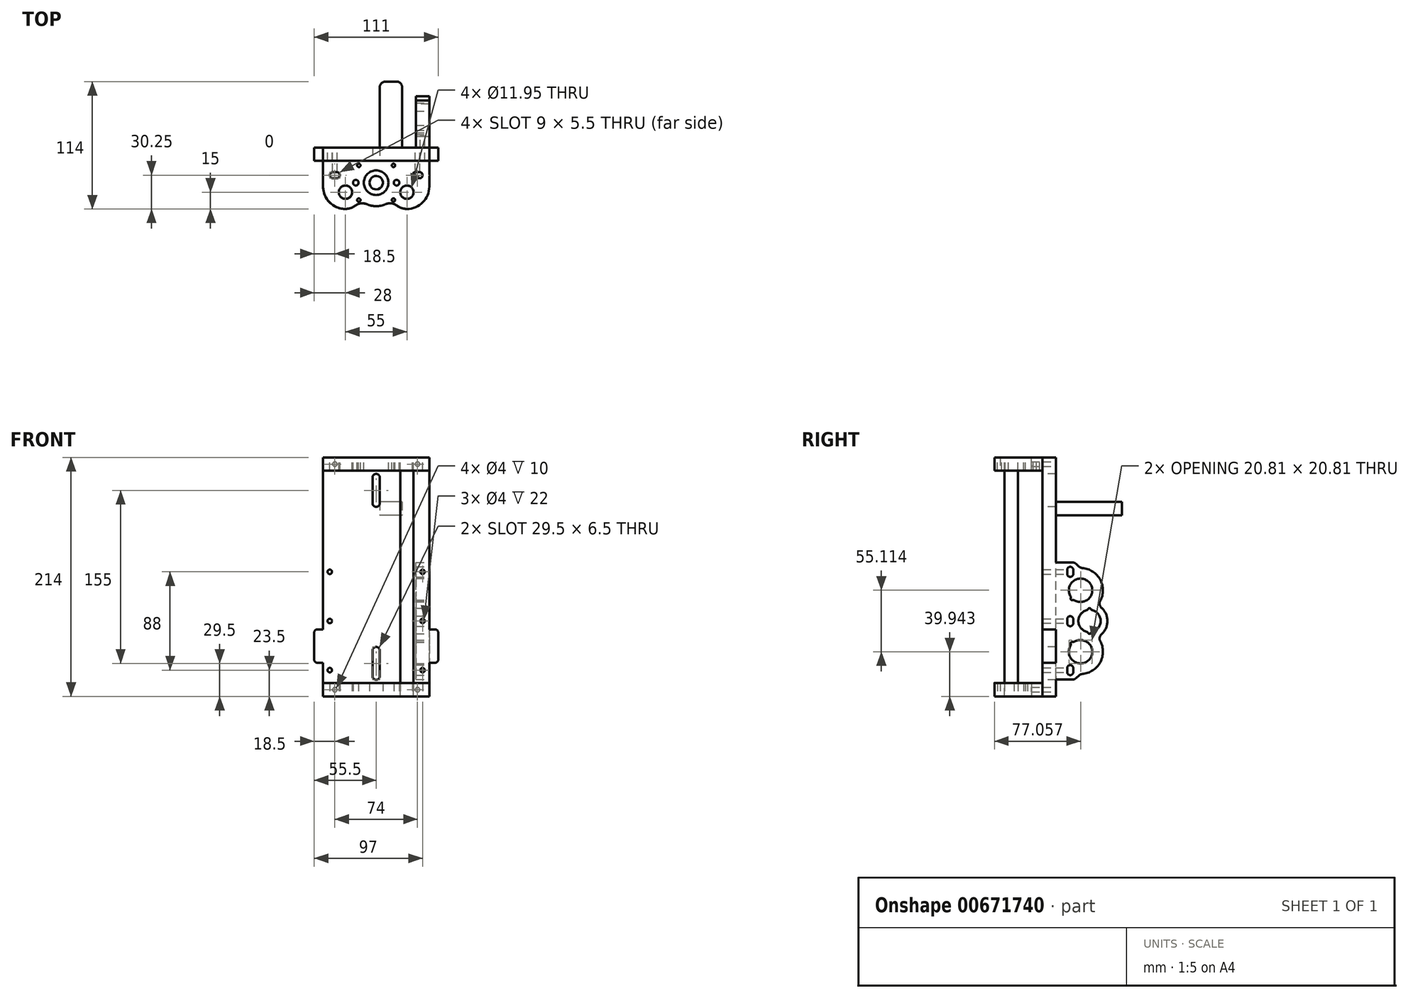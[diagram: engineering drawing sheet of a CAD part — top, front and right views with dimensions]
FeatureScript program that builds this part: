
annotation { "Feature Type Name" : "Feature", "Feature Type Description" : "" }
export const myFeature = defineFeature(function(context is Context, id is Id, definition is map)
    precondition{}
    {
        {
            assignVariable(context, id + "F0", {"name" : "L", "anyValue" : 214});
        }
        {
            var Q0;
            Q0=qCreatedBy(makeId("Front.planeOp"),FACE);
            var sketch = newSketch(context, id + "F1", { "sketchPlane" : qUnion([Q0])});
            skLineSegment(sketch, "E0.bottom", {"start": v(47.5, 0) * mm, "end": v(-47.5, 0) * mm});
            skLineSegment(sketch, "E0.top", {"start": v(-47.5, 214) * mm, "end": v(47.5, 214) * mm});
            skLineSegment(sketch, "E0.left", {"start": v(-47.5, 0) * mm, "end": v(-47.5, 214) * mm});
            skLineSegment(sketch, "E0.right", {"start": v(47.5, 0) * mm, "end": v(47.5, 214) * mm});
            skLineSegment(sketch, "E1.left", {"start": v(3.25, 196) * mm, "end": v(3.25, 173) * mm});
            skLineSegment(sketch, "E1.right", {"start": v(-3.25, 196) * mm, "end": v(-3.25, 173) * mm});
            skArc(sketch, "E2", {"start": v(3.25, 196) * mm, "mid": v(0, 199.25) * mm, "end": v(-3.25, 196) * mm});
            skArc(sketch, "E3", {"start": v(-3.25, 173) * mm, "mid": v(0, 169.75) * mm, "end": v(3.25, 173) * mm});
            skLineSegment(sketch, "E4", {"start": v(0, 214) * mm, "end": v(0, 196) * mm, "construction": true});
            skLineSegment(sketch, "E5.left", {"start": v(-3.25, 18) * mm, "end": v(-3.25, 41) * mm});
            skLineSegment(sketch, "E5.right", {"start": v(3.25, 18) * mm, "end": v(3.25, 41) * mm});
            skArc(sketch, "E6", {"start": v(-3.25, 18) * mm, "mid": v(0, 14.75) * mm, "end": v(3.25, 18) * mm});
            skArc(sketch, "E7", {"start": v(3.25, 41) * mm, "mid": v(0, 44.25) * mm, "end": v(-3.25, 41) * mm});
            skLineSegment(sketch, "E8", {"start": v(0, 0) * mm, "end": v(0, 18) * mm, "construction": true});
            skSolve(sketch);
        }
        {
            var Q0;
            Q0=qSketchRegion(id+"F1",true);
            extrude(context, id + "F2", {"entities" : qUnion([Q0]), "oppositeDirection" : true, "depth" : 12 * mm, "offsetDistance" : 25 * mm});
        }
        {
            var Q0;
            Q0=makeQuery(id+"F2.opExtrude","SWEPT_FACE",FACE,{"disambiguationData":[OSD([sQuery(id+"F1.wireOp",EDGE,"E0.top")])]});
            var sketch = newSketch(context, id + "F3", { "sketchPlane" : qUnion([Q0])});
            skLineSegment(sketch, "E9.bottom", {"start": v(-47.5, 0) * mm, "end": v(47.5, 0) * mm});
            skLineSegment(sketch, "E9.top", {"start": v(-27.5, -43) * mm, "end": v(27.5, -43) * mm, "construction": true});
            skLineSegment(sketch, "E9.left", {"start": v(-47.5, 0) * mm, "end": v(-47.5, -23) * mm});
            skLineSegment(sketch, "E9.right", {"start": v(47.5, 0) * mm, "end": v(47.5, -23) * mm});
            skLineSegment(sketch, "E10", {"start": v(0, 0) * mm, "end": v(0, -43) * mm, "construction": true});
            skCircle(sketch, "E11", {"center": v(-27.5, -28) * mm, "radius": 5.97 * mm});
            skCircle(sketch, "E12.MirrorC", {"center": v(27.5, -28) * mm, "radius": 5.97 * mm});
            skArc(sketch, "E13.filletArc", {"start": v(-47.5, -23) * mm, "mid": v(-41.64, -37.14) * mm, "end": v(-27.5, -43) * mm});
            skPoint(sketch, "E14.visualSharp", {"position": v(47.5, -43) * mm});
            skArc(sketch, "E14.filletArc", {"start": v(27.5, -43) * mm, "mid": v(41.64, -37.14) * mm, "end": v(47.5, -23) * mm});
            skCircle(sketch, "E15", {"center": v(0, -19.5) * mm, "radius": 11 * mm});
            skCircle(sketch, "E16", {"center": v(-18.25, -19.5) * mm, "radius": 2.5 * mm});
            skCircle(sketch, "E17.MirrorC", {"center": v(18.25, -19.5) * mm, "radius": 2.5 * mm});
            skLineSegment(sketch, "E18.bottom", {"start": v(-38.75, -10) * mm, "end": v(-35.25, -10) * mm});
            skLineSegment(sketch, "E18.top", {"start": v(-38.75, -15.5) * mm, "end": v(-35.25, -15.5) * mm});
            skArc(sketch, "E19", {"start": v(-38.75, -10) * mm, "mid": v(-41.5, -12.75) * mm, "end": v(-38.75, -15.5) * mm});
            skArc(sketch, "E20", {"start": v(-35.25, -15.5) * mm, "mid": v(-32.5, -12.75) * mm, "end": v(-35.25, -10) * mm});
            skLineSegment(sketch, "E21", {"start": v(-37, -10) * mm, "end": v(-37, -15.5) * mm, "construction": true});
            skArc(sketch, "E22.MirrorCS", {"start": v(35.25, -15.5) * mm, "mid": v(32.5, -12.75) * mm, "end": v(35.25, -10) * mm});
            skLineSegment(sketch, "E23.MirrorCS", {"start": v(38.75, -15.5) * mm, "end": v(35.25, -15.5) * mm});
            skLineSegment(sketch, "E24.MirrorCS", {"start": v(38.75, -10) * mm, "end": v(35.25, -10) * mm});
            skArc(sketch, "E25.MirrorCS", {"start": v(38.75, -10) * mm, "mid": v(41.5, -12.75) * mm, "end": v(38.75, -15.5) * mm});
            skArc(sketch, "E26", {"start": v(-7.8, 0) * mm, "mid": v(0, -40.5) * mm, "end": v(7.8, 0) * mm});
            skCircle(sketch, "E27", {"center": v(-27.5, -28) * mm, "radius": 15 * mm});
            skCircle(sketch, "E28", {"center": v(27.5, -28) * mm, "radius": 15 * mm});
            skSolve(sketch);
        }
        {
            var Q0;
            Q0=qSketchRegion(id+"F3",true);
            extrude(context, id + "F4", {"entities" : qUnion([Q0]), "oppositeDirection" : true, "depth" : 12 * mm, "offsetDistance" : 25 * mm});
        }
        {
            var Q0;
            Q0=makeQuery(id+"F4.opExtrude","SWEPT_EDGE",EDGE,{"disambiguationData":[OSD([sQuery(id+"F3.wireOp",EDGE,"E26"),sQuery(id+"F3.wireOp",EDGE,"E27")])]});
            var Q1;
            Q1=makeQuery(id+"F4.opExtrude","SWEPT_EDGE",EDGE,{"disambiguationData":[OSD([sQuery(id+"F3.wireOp",EDGE,"E26"),sQuery(id+"F3.wireOp",EDGE,"E28")])]});
            fillet(context, id + "F5", {"entities" : qUnion([Q0, Q1]), "radius" : 10 * mm, "tangentPropagation" : true, "allowEdgeOverflow" : false});
        }
        {
            var Q0;
            Q0=makeQuery(id+"F4.opExtrude","CAP_FACE",FACE,{"disambiguationData":[OSD([sQuery(id+"F3.wireOp",EDGE,"E9.bottom"),sQuery(id+"F3.wireOp",EDGE,"E9.top"),sQuery(id+"F3.wireOp",EDGE,"E9.left"),sQuery(id+"F3.wireOp",EDGE,"E9.right"),sQuery(id+"F3.wireOp",EDGE,"E11"),sQuery(id+"F3.wireOp",EDGE,"E12.MirrorC"),sQuery(id+"F3.wireOp",EDGE,"E13.filletArc"),sQuery(id+"F3.wireOp",EDGE,"E14.filletArc")])],"isStart":true});
            var sketch = newSketch(context, id + "F6", { "sketchPlane" : qUnion([Q0])});
            skCircle(sketch, "E29", {"center": v(27.5, -28) * mm, "radius": 6 * mm});
            skSolve(sketch);
        }
        {
            var Q0;
            Q0=qSketchRegion(id+"F6",true);
            extrude(context, id + "F7", {"entities" : qUnion([Q0]), "oppositeDirection" : true, "depth" : (getVariable(context, 'L')) * mm, "offsetDistance" : 25 * mm});
        }
        {
            var Q0;
            Q0=makeQuery(id+"F2.opExtrude","SWEPT_FACE",FACE,{"disambiguationData":[OSD([sQuery(id+"F1.wireOp",EDGE,"E0.right")])]});
            var sketch = newSketch(context, id + "F8", { "sketchPlane" : qUnion([Q0])});
            skLineSegment(sketch, "E30.top", {"start": v(54, 40) * mm, "end": v(54, 67.5) * mm, "construction": true});
            skLineSegment(sketch, "E31", {"start": v(12, 67.5) * mm, "end": v(54, 67.5) * mm, "construction": true});
            skArc(sketch, "E32.filletArc", {"start": v(34, 20) * mm, "mid": v(48.14, 25.86) * mm, "end": v(54, 40) * mm});
            skArc(sketch, "E33.filletArc", {"start": v(54, 95) * mm, "mid": v(48.14, 109.14) * mm, "end": v(34, 115) * mm});
            skArc(sketch, "E34", {"start": v(25.22, 45.7) * mm, "mid": v(41.4, 32.6) * mm, "end": v(28.3, 48.78) * mm});
            skArc(sketch, "E35.MirrorC", {"start": v(25.22, 89.3) * mm, "mid": v(41.4, 102.4) * mm, "end": v(28.3, 86.22) * mm});
            skArc(sketch, "E36", {"start": v(49.07, 53.15) * mm, "mid": v(58, 67.5) * mm, "end": v(49.07, 81.85) * mm});
            skArc(sketch, "E37", {"start": v(39.83, 77.24) * mm, "mid": v(32.03, 67.5) * mm, "end": v(39.83, 57.76) * mm});
            skLineSegment(sketch, "E38.bottom", {"start": v(34, 20) * mm, "end": v(28.5, 15) * mm});
            skLineSegment(sketch, "E38.right", {"start": v(28.5, 15) * mm, "end": v(12, 15) * mm});
            skLineSegment(sketch, "E39.bottom", {"start": v(27.5, 25.25) * mm, "end": v(27.5, 21.75) * mm});
            skLineSegment(sketch, "E39.top", {"start": v(22, 25.25) * mm, "end": v(22, 21.75) * mm});
            skArc(sketch, "E40", {"start": v(27.5, 25.25) * mm, "mid": v(24.75, 28) * mm, "end": v(22, 25.25) * mm});
            skArc(sketch, "E41", {"start": v(22, 21.75) * mm, "mid": v(24.75, 19) * mm, "end": v(27.5, 21.75) * mm});
            skLineSegment(sketch, "E42.MirrorCS", {"start": v(34, 115) * mm, "end": v(28.5, 120) * mm});
            skLineSegment(sketch, "E43.MirrorCS", {"start": v(28.5, 120) * mm, "end": v(12, 120) * mm});
            skLineSegment(sketch, "E44.top", {"start": v(22, 69.07) * mm, "end": v(22, 65.57) * mm});
            skArc(sketch, "E45", {"start": v(27.5, 69.07) * mm, "mid": v(24.75, 71.82) * mm, "end": v(22, 69.07) * mm});
            skArc(sketch, "E46", {"start": v(22, 65.57) * mm, "mid": v(24.75, 62.82) * mm, "end": v(27.5, 65.57) * mm});
            skLineSegment(sketch, "E47", {"start": v(22, 23.5) * mm, "end": v(27.5, 23.5) * mm, "construction": true});
            skLineSegment(sketch, "E48.trimOffspring", {"start": v(54, 67.5) * mm, "end": v(54, 95) * mm, "construction": true});
            skLineSegment(sketch, "E49", {"start": v(12, 120) * mm, "end": v(12, 15) * mm});
            skLineSegment(sketch, "E50", {"start": v(34, 40) * mm, "end": v(34, 20) * mm, "construction": true});
            skLineSegment(sketch, "E51", {"start": v(34, 95) * mm, "end": v(34, 40) * mm, "construction": true});
            skArc(sketch, "E52", {"start": v(54, 40) * mm, "mid": v(52.73, 47.02) * mm, "end": v(49.07, 53.15) * mm});
            skArc(sketch, "E53.MirrorCS", {"start": v(54, 95) * mm, "mid": v(52.73, 87.98) * mm, "end": v(49.07, 81.85) * mm});
            skLineSegment(sketch, "E54", {"start": v(34, 95) * mm, "end": v(26.6, 87.6) * mm, "construction": true});
            skArc(sketch, "E55", {"start": v(25.26, 88.29) * mm, "mid": v(25.53, 86.53) * mm, "end": v(27.29, 86.26) * mm});
            skPoint(sketch, "E56.visualSharp", {"position": v(25.61, 88.73) * mm});
            skArc(sketch, "E56.filletArc", {"start": v(25.26, 88.29) * mm, "mid": v(25.38, 88.8) * mm, "end": v(25.22, 89.3) * mm});
            skPoint(sketch, "E57.visualSharp", {"position": v(27.73, 86.61) * mm});
            skArc(sketch, "E57.filletArc", {"start": v(28.3, 86.22) * mm, "mid": v(27.8, 86.38) * mm, "end": v(27.29, 86.26) * mm});
            skArc(sketch, "E58.MirrorCS", {"start": v(28.3, 48.78) * mm, "mid": v(27.8, 48.62) * mm, "end": v(27.29, 48.74) * mm});
            skArc(sketch, "E59.MirrorCS", {"start": v(25.26, 46.71) * mm, "mid": v(25.53, 48.47) * mm, "end": v(27.29, 48.74) * mm});
            skArc(sketch, "E60.MirrorCS", {"start": v(25.26, 46.71) * mm, "mid": v(25.38, 46.2) * mm, "end": v(25.22, 45.7) * mm});
            skLineSegment(sketch, "E61", {"start": v(27.5, 69.07) * mm, "end": v(27.5, 65.57) * mm});
            skArc(sketch, "E62.MirrorCS", {"start": v(27.5, 109.75) * mm, "mid": v(24.75, 107) * mm, "end": v(22, 109.75) * mm});
            skLineSegment(sketch, "E63.MirrorCS", {"start": v(27.5, 109.75) * mm, "end": v(27.5, 113.25) * mm});
            skLineSegment(sketch, "E64.MirrorCS", {"start": v(22, 109.75) * mm, "end": v(22, 113.25) * mm});
            skArc(sketch, "E65.MirrorCS", {"start": v(22, 113.25) * mm, "mid": v(24.75, 116) * mm, "end": v(27.5, 113.25) * mm});
            skArc(sketch, "E66", {"start": v(43.43, 77.92) * mm, "mid": v(42, 78.97) * mm, "end": v(40.57, 77.92) * mm});
            skArc(sketch, "E67.filletArc", {"start": v(43.43, 77.92) * mm, "mid": v(43.71, 77.48) * mm, "end": v(44.17, 77.24) * mm});
            skArc(sketch, "E68.filletArc", {"start": v(39.83, 77.24) * mm, "mid": v(40.29, 77.48) * mm, "end": v(40.57, 77.92) * mm});
            skArc(sketch, "E69.MirrorCS", {"start": v(43.43, 57.08) * mm, "mid": v(43.71, 57.52) * mm, "end": v(44.17, 57.76) * mm});
            skArc(sketch, "E70.MirrorCS", {"start": v(43.43, 57.08) * mm, "mid": v(42, 56.02) * mm, "end": v(40.57, 57.08) * mm});
            skArc(sketch, "E71.MirrorCS", {"start": v(39.83, 57.76) * mm, "mid": v(40.29, 57.52) * mm, "end": v(40.57, 57.08) * mm});
            skArc(sketch, "E72.trimOffspring", {"start": v(44.17, 57.76) * mm, "mid": v(51.98, 67.5) * mm, "end": v(44.17, 77.24) * mm});
            skCircle(sketch, "E73", {"center": v(42, 67.5) * mm, "radius": 9.97 * mm, "construction": true});
            skSolve(sketch);
        }
        {
            var Q0;
            Q0=qSketchRegion(id+"F8",true);
            extrude(context, id + "F9", {"entities" : qUnion([Q0]), "oppositeDirection" : true, "depth" : 12 * mm, "offsetDistance" : 25 * mm});
        }
        {
            var Q0;
            Q0=makeQuery(id+"F2.opExtrude","SWEPT_FACE",FACE,{"disambiguationData":[OSD([sQuery(id+"F1.wireOp",EDGE,"E0.bottom")])]});
            var sketch = newSketch(context, id + "F10", { "sketchPlane" : qUnion([Q0])});
            skLineSegment(sketch, "E74.0", {"start": v(-47.5, 0) * mm, "end": v(47.5, 0) * mm});
            skArc(sketch, "E74.1", {"start": v(47.5, 23) * mm, "mid": v(41.64, 37.14) * mm, "end": v(27.5, 43) * mm});
            skLineSegment(sketch, "E74.3", {"start": v(47.5, 0) * mm, "end": v(47.5, 23) * mm});
            skArc(sketch, "E74.4", {"start": v(-27.5, 43) * mm, "mid": v(-41.64, 37.14) * mm, "end": v(-47.5, 23) * mm});
            skLineSegment(sketch, "E74.5", {"start": v(-47.5, 23) * mm, "end": v(-47.5, 0) * mm});
            skCircle(sketch, "E75.0", {"center": v(-27.5, 28) * mm, "radius": 5.97 * mm});
            skCircle(sketch, "E76.0", {"center": v(27.5, 28) * mm, "radius": 5.97 * mm});
            skCircle(sketch, "E77.0", {"center": v(-18.25, 19.5) * mm, "radius": 2.5 * mm});
            skCircle(sketch, "E78.0", {"center": v(18.25, 19.5) * mm, "radius": 2.5 * mm});
            skCircle(sketch, "E79.0", {"center": v(0, 19.5) * mm, "radius": 6 * mm});
            skArc(sketch, "E80.0", {"start": v(18.43, 39.95) * mm, "mid": v(22.72, 42.22) * mm, "end": v(27.5, 43) * mm});
            skArc(sketch, "E80.1", {"start": v(-27.5, 43) * mm, "mid": v(-22.72, 42.22) * mm, "end": v(-18.43, 39.95) * mm});
            skArc(sketch, "E80.2", {"start": v(-18.43, 39.95) * mm, "mid": v(-13.58, 37.99) * mm, "end": v(-8.4, 38.75) * mm});
            skArc(sketch, "E80.3", {"start": v(-8.4, 38.75) * mm, "mid": v(0, 40.5) * mm, "end": v(8.4, 38.75) * mm});
            skArc(sketch, "E80.4", {"start": v(8.4, 38.75) * mm, "mid": v(13.58, 37.99) * mm, "end": v(18.43, 39.95) * mm});
            skArc(sketch, "E81.0", {"start": v(-38.75, 10) * mm, "mid": v(-41.5, 12.75) * mm, "end": v(-38.75, 15.5) * mm});
            skLineSegment(sketch, "E81.1", {"start": v(-38.75, 10) * mm, "end": v(-35.25, 10) * mm});
            skArc(sketch, "E81.2", {"start": v(-35.25, 15.5) * mm, "mid": v(-32.5, 12.75) * mm, "end": v(-35.25, 10) * mm});
            skLineSegment(sketch, "E81.3", {"start": v(-38.75, 15.5) * mm, "end": v(-35.25, 15.5) * mm});
            skArc(sketch, "E82.0", {"start": v(35.25, 15.5) * mm, "mid": v(32.5, 12.75) * mm, "end": v(35.25, 10) * mm});
            skLineSegment(sketch, "E82.1", {"start": v(38.75, 15.5) * mm, "end": v(35.25, 15.5) * mm});
            skArc(sketch, "E82.2", {"start": v(38.75, 10) * mm, "mid": v(41.5, 12.75) * mm, "end": v(38.75, 15.5) * mm});
            skLineSegment(sketch, "E82.3", {"start": v(38.75, 10) * mm, "end": v(35.25, 10) * mm});
            skSolve(sketch);
        }
        {
            var Q0;
            Q0=qSketchRegion(id+"F10",true);
            extrude(context, id + "F11", {"entities" : qUnion([Q0]), "oppositeDirection" : true, "depth" : 12 * mm, "offsetDistance" : 25 * mm});
        }
        {
            var Q0;
            Q0=makeQuery(id+"F2.opExtrude","CAP_FACE",FACE,{"disambiguationData":[OSD([sQuery(id+"F1.wireOp",EDGE,"E0.bottom"),sQuery(id+"F1.wireOp",EDGE,"E0.top"),sQuery(id+"F1.wireOp",EDGE,"E0.left"),sQuery(id+"F1.wireOp",EDGE,"E0.right")])],"isStart":false});
            var sketch = newSketch(context, id + "F12", { "sketchPlane" : qUnion([Q0])});
            skCircle(sketch, "E83", {"center": v(-37, 208) * mm, "radius": 2 * mm});
            skCircle(sketch, "E84", {"center": v(37, 208) * mm, "radius": 2 * mm});
            skLineSegment(sketch, "E85", {"start": v(-47.5, 107) * mm, "end": v(47.5, 107) * mm, "construction": true});
            skCircle(sketch, "E86.MirrorC", {"center": v(37, 6) * mm, "radius": 2 * mm});
            skCircle(sketch, "E87.MirrorC", {"center": v(-37, 6) * mm, "radius": 2 * mm});
            skCircle(sketch, "E88", {"center": v(-41.5, 23.5) * mm, "radius": 2 * mm});
            skCircle(sketch, "E89", {"center": v(-41.5, 111.5) * mm, "radius": 2 * mm});
            skCircle(sketch, "E90", {"center": v(-41.5, 67.5) * mm, "radius": 2 * mm});
            skLineSegment(sketch, "E91", {"start": v(0, 107) * mm, "end": v(0, 0) * mm, "construction": true});
            skCircle(sketch, "E92.MirrorC", {"center": v(41.5, 23.5) * mm, "radius": 2 * mm});
            skCircle(sketch, "E93.MirrorC", {"center": v(41.5, 111.5) * mm, "radius": 2 * mm});
            skCircle(sketch, "E94.MirrorC", {"center": v(41.5, 67.5) * mm, "radius": 2 * mm});
            skSolve(sketch);
        }
        {
            var Q0;
            Q0=qSketchRegion(id+"F12",true);
            extrude(context, id + "F13", {"entities" : qUnion([Q0]), "operationType" : NewBodyOperationType.REMOVE, "oppositeDirection" : true, "depth" : 25 * mm, "offsetDistance" : 25 * mm, "hasSecondDirection" : true, "secondDirectionOppositeDirection" : false, "secondDirectionDepth" : 10 * mm});
        }
        {
            var Q0;
            Q0=makeQuery(id+"F4.opExtrude","CAP_FACE",FACE,{"disambiguationData":[OSD([sQuery(id+"F3.wireOp",EDGE,"E9.bottom"),sQuery(id+"F3.wireOp",EDGE,"E9.left"),sQuery(id+"F3.wireOp",EDGE,"E9.right"),sQuery(id+"F3.wireOp",EDGE,"E11"),sQuery(id+"F3.wireOp",EDGE,"E12.MirrorC"),sQuery(id+"F3.wireOp",EDGE,"E13.filletArc"),sQuery(id+"F3.wireOp",EDGE,"E14.filletArc"),sQuery(id+"F3.wireOp",EDGE,"E15"),sQuery(id+"F3.wireOp",EDGE,"E16"),sQuery(id+"F3.wireOp",EDGE,"E17.MirrorC"),sQuery(id+"F3.wireOp",EDGE,"E18.bottom"),sQuery(id+"F3.wireOp",EDGE,"E18.top"),sQuery(id+"F3.wireOp",EDGE,"E19"),sQuery(id+"F3.wireOp",EDGE,"E20"),sQuery(id+"F3.wireOp",EDGE,"E22.MirrorCS"),sQuery(id+"F3.wireOp",EDGE,"E23.MirrorCS"),sQuery(id+"F3.wireOp",EDGE,"E24.MirrorCS"),sQuery(id+"F3.wireOp",EDGE,"E25.MirrorCS"),sQuery(id+"F3.wireOp",EDGE,"E26"),sQuery(id+"F3.wireOp",EDGE,"E27"),sQuery(id+"F3.wireOp",EDGE,"E28")])],"isStart":true});
            var sketch = newSketch(context, id + "F14", { "sketchPlane" : qUnion([Q0])});
            skLineSegment(sketch, "E95.bottom", {"start": v(-15.5, -4) * mm, "end": v(15.5, -4) * mm, "construction": true});
            skLineSegment(sketch, "E95.top", {"start": v(-15.5, -35) * mm, "end": v(15.5, -35) * mm, "construction": true});
            skLineSegment(sketch, "E95.left", {"start": v(-15.5, -4) * mm, "end": v(-15.5, -35) * mm, "construction": true});
            skLineSegment(sketch, "E95.right", {"start": v(15.5, -4) * mm, "end": v(15.5, -35) * mm, "construction": true});
            skLineSegment(sketch, "E96", {"start": v(-15.5, -19.5) * mm, "end": v(15.5, -19.5) * mm, "construction": true});
            skPoint(sketch, "E97", {"position": v(0, -19.5) * mm});
            skCircle(sketch, "E98", {"center": v(-15.5, -4) * mm, "radius": 1.5 * mm});
            skCircle(sketch, "E99.1.0", {"center": v(-15.5, -35) * mm, "radius": 1.5 * mm});
            skCircle(sketch, "E99.2.0", {"center": v(15.5, -35) * mm, "radius": 1.5 * mm});
            skCircle(sketch, "E99.3.0", {"center": v(15.5, -4) * mm, "radius": 1.5 * mm});
            skLineSegment(sketch, "E100", {"start": v(-15.5, -4) * mm, "end": v(15.5, -35) * mm, "construction": true});
            skSolve(sketch);
        }
        {
            var Q0;
            Q0=qSketchRegion(id+"F14",true);
            extrude(context, id + "F15", {"entities" : qUnion([Q0]), "operationType" : NewBodyOperationType.REMOVE, "oppositeDirection" : true, "depth" : 25 * mm, "offsetDistance" : 25 * mm});
        }
        {
            var Q0;
            Q0=makeQuery(id+"F9.opExtrude","SWEPT_EDGE",EDGE,{"disambiguationData":[OSD([sQuery(id+"F8.wireOp",EDGE,"E32.filletArc"),sQuery(id+"F8.wireOp",EDGE,"E38.bottom")])]});
            var Q1;
            Q1=makeQuery(id+"F9.opExtrude","SWEPT_EDGE",EDGE,{"disambiguationData":[OSD([sQuery(id+"F8.wireOp",EDGE,"E38.bottom"),sQuery(id+"F8.wireOp",EDGE,"E38.right")])]});
            var Q2;
            Q2=makeQuery(id+"F9.opExtrude","SWEPT_EDGE",EDGE,{"disambiguationData":[OSD([sQuery(id+"F8.wireOp",EDGE,"E33.filletArc"),sQuery(id+"F8.wireOp",EDGE,"E42.MirrorCS")])]});
            var Q3;
            Q3=makeQuery(id+"F9.opExtrude","SWEPT_EDGE",EDGE,{"disambiguationData":[OSD([sQuery(id+"F8.wireOp",EDGE,"E42.MirrorCS"),sQuery(id+"F8.wireOp",EDGE,"E43.MirrorCS")])]});
            fillet(context, id + "F16", {"entities" : qUnion([Q0, Q1, Q2, Q3]), "radius" : 5 * mm, "tangentPropagation" : true, "allowEdgeOverflow" : false});
        }
        {
            var Q0;
            Q0=makeQuery(id+"F9.opExtrude","SWEPT_EDGE",EDGE,{"disambiguationData":[OSD([sQuery(id+"F8.wireOp",EDGE,"E36"),sQuery(id+"F8.wireOp",EDGE,"E53.MirrorCS")])]});
            var Q1;
            Q1=makeQuery(id+"F9.opExtrude","SWEPT_EDGE",EDGE,{"disambiguationData":[OSD([sQuery(id+"F8.wireOp",EDGE,"E36"),sQuery(id+"F8.wireOp",EDGE,"E52")])]});
            var Q2;
            Q2=makeQuery(id+"F9.opExtrude","SWEPT_EDGE",EDGE,{"disambiguationData":[OSD([sQuery(id+"F8.wireOp",EDGE,"E37"),sQuery(id+"F8.wireOp",EDGE,"E44.bottom"),sQuery(id+"F8.wireOp",EDGE,"E45")])]});
            var Q3;
            Q3=makeQuery(id+"F9.opExtrude","SWEPT_EDGE",EDGE,{"disambiguationData":[OSD([sQuery(id+"F8.wireOp",EDGE,"E37"),sQuery(id+"F8.wireOp",EDGE,"E44.bottom"),sQuery(id+"F8.wireOp",EDGE,"E46")])]});
            fillet(context, id + "F17", {"entities" : qUnion([Q0, Q1, Q2, Q3]), "radius" : 5 * mm, "tangentPropagation" : true, "allowEdgeOverflow" : false});
        }
        {
            var Q0;
            Q0=makeQuery(id+"F2.opExtrude","CAP_FACE",FACE,{"disambiguationData":[OSD([sQuery(id+"F1.wireOp",EDGE,"E0.bottom"),sQuery(id+"F1.wireOp",EDGE,"E0.top"),sQuery(id+"F1.wireOp",EDGE,"E0.left"),sQuery(id+"F1.wireOp",EDGE,"E0.right"),sQuery(id+"F1.wireOp",EDGE,"E1.left"),sQuery(id+"F1.wireOp",EDGE,"E1.right"),sQuery(id+"F1.wireOp",EDGE,"E2"),sQuery(id+"F1.wireOp",EDGE,"E3"),sQuery(id+"F1.wireOp",EDGE,"E5.left"),sQuery(id+"F1.wireOp",EDGE,"E5.right"),sQuery(id+"F1.wireOp",EDGE,"E6"),sQuery(id+"F1.wireOp",EDGE,"E7")])],"isStart":false});
            var sketch = newSketch(context, id + "F18", { "sketchPlane" : qUnion([Q0])});
            skLineSegment(sketch, "E101.bottom", {"start": v(47.5, 30) * mm, "end": v(55.5, 30) * mm});
            skLineSegment(sketch, "E101.top", {"start": v(47.5, 60) * mm, "end": v(55.5, 60) * mm});
            skLineSegment(sketch, "E101.left", {"start": v(47.5, 30) * mm, "end": v(47.5, 60) * mm});
            skLineSegment(sketch, "E101.right", {"start": v(55.5, 30) * mm, "end": v(55.5, 60) * mm});
            skLineSegment(sketch, "E102", {"start": v(0, 18) * mm, "end": v(0, 41) * mm, "construction": true});
            skLineSegment(sketch, "E103.MirrorCS", {"start": v(-47.5, 60) * mm, "end": v(-55.5, 60) * mm});
            skLineSegment(sketch, "E104.MirrorCS", {"start": v(-47.5, 30) * mm, "end": v(-47.5, 60) * mm});
            skLineSegment(sketch, "E105.MirrorCS", {"start": v(-55.5, 30) * mm, "end": v(-55.5, 60) * mm});
            skLineSegment(sketch, "E106.MirrorCS", {"start": v(-47.5, 30) * mm, "end": v(-55.5, 30) * mm});
            skSolve(sketch);
        }
        {
            var Q0;
            Q0=qSketchRegion(id+"F18",true);
            extrude(context, id + "F19", {"entities" : qUnion([Q0]), "operationType" : NewBodyOperationType.ADD, "oppositeDirection" : true, "depth" : 12 * mm, "offsetDistance" : 25 * mm});
        }
        {
            var Q0;
            Q0=makeQuery(id+"F19.opExtrude","SWEPT_EDGE",EDGE,{"disambiguationData":[OSD([sQuery(id+"F1.wireOp",EDGE,"E0.left"),sQuery(id+"F18.wireOp",EDGE,"E101.top"),sQuery(id+"F18.wireOp",EDGE,"E101.left")])]});
            var Q1;
            Q1=makeQuery(id+"F19.opExtrude","SWEPT_EDGE",EDGE,{"disambiguationData":[OSD([sQuery(id+"F1.wireOp",EDGE,"E0.left"),sQuery(id+"F18.wireOp",EDGE,"E101.bottom"),sQuery(id+"F18.wireOp",EDGE,"E101.left")])]});
            var Q2;
            Q2=makeQuery(id+"F19.opExtrude","SWEPT_EDGE",EDGE,{"disambiguationData":[OSD([sQuery(id+"F18.wireOp",EDGE,"E101.bottom"),sQuery(id+"F18.wireOp",EDGE,"E101.right")])]});
            var Q3;
            Q3=makeQuery(id+"F19.opExtrude","SWEPT_EDGE",EDGE,{"disambiguationData":[OSD([sQuery(id+"F18.wireOp",EDGE,"E101.top"),sQuery(id+"F18.wireOp",EDGE,"E101.right")])]});
            var Q4;
            Q4=makeQuery(id+"F19.opExtrude","SWEPT_EDGE",EDGE,{"disambiguationData":[OSD([sQuery(id+"F18.wireOp",EDGE,"E105.MirrorCS"),sQuery(id+"F18.wireOp",EDGE,"E106.MirrorCS")])]});
            var Q5;
            Q5=makeQuery(id+"F19.opExtrude","SWEPT_EDGE",EDGE,{"disambiguationData":[OSD([sQuery(id+"F1.wireOp",EDGE,"E0.right"),sQuery(id+"F18.wireOp",EDGE,"E104.MirrorCS"),sQuery(id+"F18.wireOp",EDGE,"E106.MirrorCS")])]});
            var Q6;
            Q6=makeQuery(id+"F19.opExtrude","SWEPT_EDGE",EDGE,{"disambiguationData":[OSD([sQuery(id+"F18.wireOp",EDGE,"E103.MirrorCS"),sQuery(id+"F18.wireOp",EDGE,"E105.MirrorCS")])]});
            var Q7;
            Q7=makeQuery(id+"F19.opExtrude","SWEPT_EDGE",EDGE,{"disambiguationData":[OSD([sQuery(id+"F1.wireOp",EDGE,"E0.right"),sQuery(id+"F18.wireOp",EDGE,"E103.MirrorCS"),sQuery(id+"F18.wireOp",EDGE,"E104.MirrorCS")])]});
            fillet(context, id + "F20", {"entities" : qUnion([Q0, Q1, Q2, Q3, Q4, Q5, Q6, Q7]), "radius" : 3 * mm, "tangentPropagation" : true, "allowEdgeOverflow" : false});
        }
        {
            var Q0;
            Q0=makeQuery(id+"F19.boolean.opBoolean","MERGE",FACE,{"derivedFrom":[makeQuery(id+"F2.opExtrude","CAP_FACE",FACE,{"disambiguationData":[OSD([sQuery(id+"F1.wireOp",EDGE,"E0.bottom"),sQuery(id+"F1.wireOp",EDGE,"E0.top"),sQuery(id+"F1.wireOp",EDGE,"E0.left"),sQuery(id+"F1.wireOp",EDGE,"E0.right"),sQuery(id+"F1.wireOp",EDGE,"E1.left"),sQuery(id+"F1.wireOp",EDGE,"E1.right"),sQuery(id+"F1.wireOp",EDGE,"E2"),sQuery(id+"F1.wireOp",EDGE,"E3"),sQuery(id+"F1.wireOp",EDGE,"E5.left"),sQuery(id+"F1.wireOp",EDGE,"E5.right"),sQuery(id+"F1.wireOp",EDGE,"E6"),sQuery(id+"F1.wireOp",EDGE,"E7")])],"isStart":false}),makeQuery(id+"F19.opExtrude","CAP_FACE",FACE,{"disambiguationData":[OSD([sQuery(id+"F18.wireOp",EDGE,"E101.bottom"),sQuery(id+"F18.wireOp",EDGE,"E101.top"),sQuery(id+"F18.wireOp",EDGE,"E101.left"),sQuery(id+"F18.wireOp",EDGE,"E101.right")])],"isStart":true}),makeQuery(id+"F19.opExtrude","CAP_FACE",FACE,{"disambiguationData":[OSD([sQuery(id+"F18.wireOp",EDGE,"E103.MirrorCS"),sQuery(id+"F18.wireOp",EDGE,"E104.MirrorCS"),sQuery(id+"F18.wireOp",EDGE,"E105.MirrorCS"),sQuery(id+"F18.wireOp",EDGE,"E106.MirrorCS")])],"isStart":true})]});
            var sketch = newSketch(context, id + "F21", { "sketchPlane" : qUnion([Q0])});
            skLineSegment(sketch, "E107.bottom", {"start": v(-23.25, 174.2) * mm, "end": v(-3.25, 174.2) * mm});
            skLineSegment(sketch, "E107.top", {"start": v(-23.25, 162.2) * mm, "end": v(-3.25, 162.2) * mm});
            skLineSegment(sketch, "E107.left", {"start": v(-23.25, 174.2) * mm, "end": v(-23.25, 162.2) * mm});
            skLineSegment(sketch, "E107.right", {"start": v(-3.25, 174.2) * mm, "end": v(-3.25, 162.2) * mm});
            skLineSegment(sketch, "E108", {"start": v(0, 174.2) * mm, "end": v(0, 214) * mm, "construction": true});
            skSolve(sketch);
        }
        {
            var Q0;
            Q0=qSketchRegion(id+"F21",true);
            extrude(context, id + "F22", {"entities" : qUnion([Q0]), "depth" : 59 * mm, "offsetDistance" : 25 * mm});
        }
        {
            var Q0;
            Q0=makeQuery(id+"F22.opExtrude","CAP_EDGE",EDGE,{"disambiguationData":[OSD([sQuery(id+"F21.wireOp",EDGE,"E107.right")])],"isStart":false});
            var Q1;
            Q1=makeQuery(id+"F22.opExtrude","CAP_EDGE",EDGE,{"disambiguationData":[OSD([sQuery(id+"F21.wireOp",EDGE,"E107.left")])],"isStart":false});
            fillet(context, id + "F23", {"entities" : qUnion([Q0, Q1]), "radius" : 5 * mm, "tangentPropagation" : true, "allowEdgeOverflow" : false});
        }
    });
